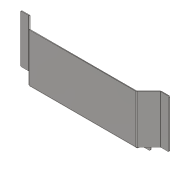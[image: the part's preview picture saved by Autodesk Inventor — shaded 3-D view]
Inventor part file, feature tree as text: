
AUTODESK INVENTOR PART (.ipt)
format: ipt  version: 2020 (Build 240168000, 168)  size: 251,392 bytes
history: native  units: mm
features: sheet_metal_op x13, other x7, sketch x6, fillet x1, projected_geometry x1
ambient origin geometry x8: Origin, YZ Plane, XZ Plane, XY Plane, X Axis, Y Axis, Z Axis, Center Point
bodies: Solid1 (feature_tree)
feature tree (28):
  sheet_metal_op  "Face1"
  sheet_metal_op  "Flange1"
  sheet_metal_op  "Flange2"
  sheet_metal_op  "Flange3"
  sheet_metal_op  "Flange4"
  fillet  "Fillet2"  Radius=245.0mm
  sketch  "Sketch1"  dims[d1=15.0mm]
  other  "Plate1"
  sketch  "Sketch2"  dims[d2=2.0mm]
  other  "Plate2"
  sheet_metal_op  "Bend1"
  sheet_metal_op  "Corner1"
  sketch  "Sketch3"  dims[d3=2.0mm]
  other  "Plate3"
  sheet_metal_op  "Bend2"
  sheet_metal_op  "Corner2"
  sketch  "Sketch4"  dims[d4=1.0mm]
  projected_geometry  "Projected Loop1"
  sketch  "Sketch6"  dims[d5=4.0mm]
  other  "Plate4"
  sheet_metal_op  "Bend3"
  sheet_metal_op  "Corner3"
  sketch  "Sketch7"  dims[d6=2.0mm d7=32.152mm d8=13.962634mm d9=1.0mm d10=8.0mm d11=2.0mm d12=2.0mm d13=2.0mm d14=1.0mm d15=4.0mm d16=2.0mm d17=112.264mm d18=13.962634mm d19=1.0mm d20=8.0mm d21=2.0mm d22=2.0mm d23=7.0mm d24=30.0mm d26=55.0mm d27=10.0mm d29=10.0mm d31=30.0mm d33=55.0mm d34=10.0mm d36=10.0mm d38=2.0mm d39=0.0mm d48=2.0mm d49=1.0mm d50=4.0mm d51=2.0mm d52=39.95mm d53=45.0deg d54=2.0mm d55=8.0mm d56=2.0mm d57=2.0mm d58=2.0mm d59=1.0mm d60=4.0mm d61=2.0mm d62=20.0mm d63=45.0deg d64=2.0mm d65=8.0mm d66=2.0mm d67=2.0mm d68=2.0mm]
  other  "Plate5"
  sheet_metal_op  "Bend4"
  sheet_metal_op  "Corner4"
  other  "Cut1"
  other  "Definition1"
